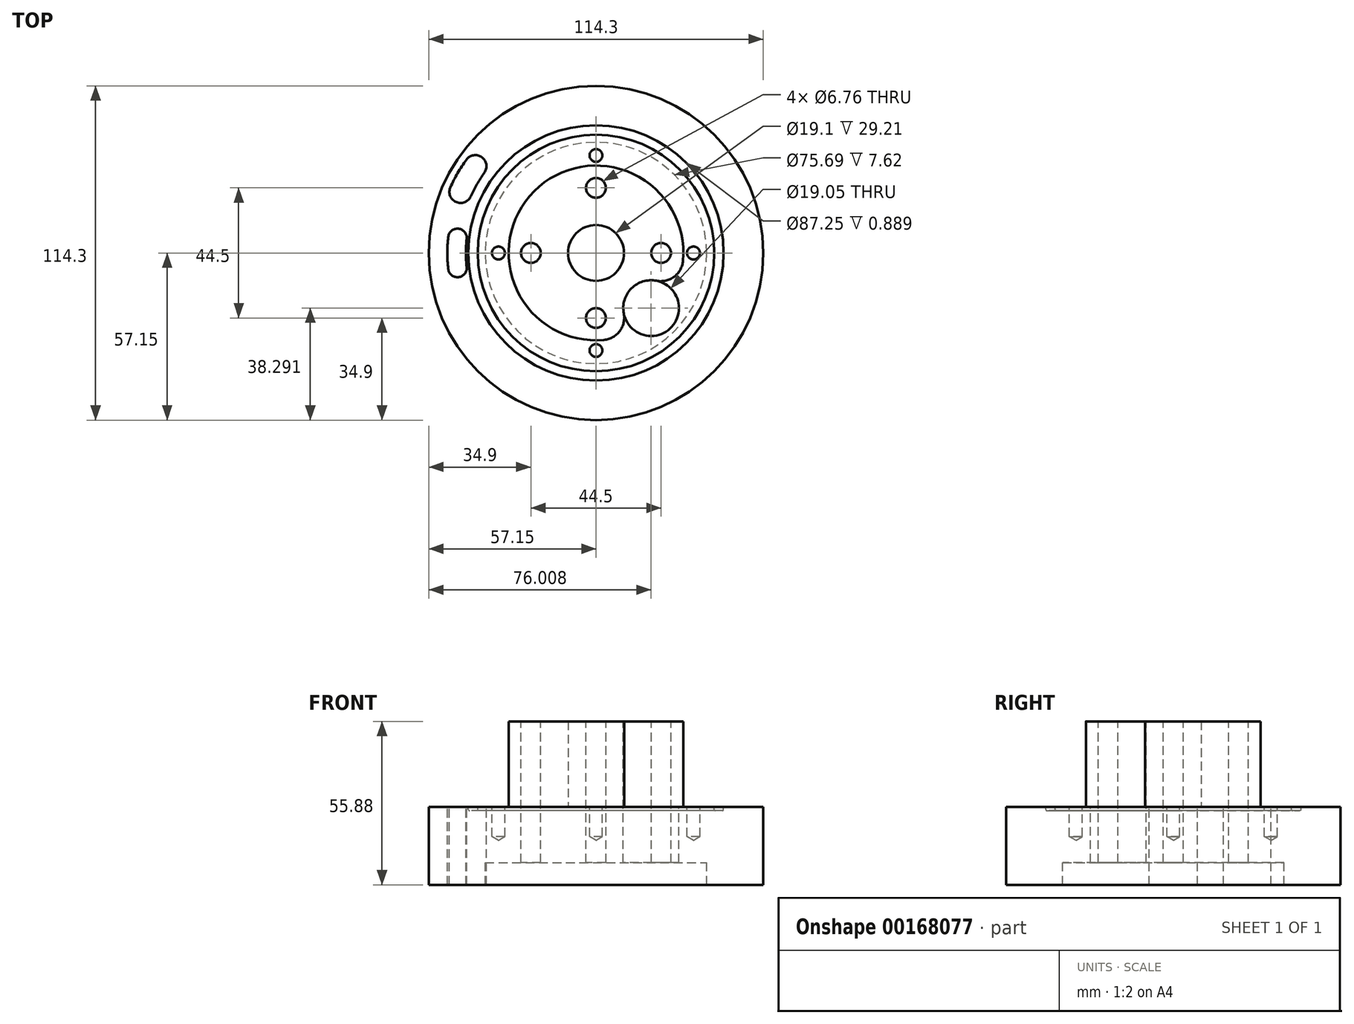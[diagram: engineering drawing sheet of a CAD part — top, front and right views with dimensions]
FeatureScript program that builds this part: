
annotation { "Feature Type Name" : "Feature", "Feature Type Description" : "" }
export const myFeature = defineFeature(function(context is Context, id is Id, definition is map)
    precondition{}
    {
        {
            var Q0;
            Q0=qCreatedBy(makeId("Top.planeOp"),FACE);
            var sketch = newSketch(context, id + "F0", { "sketchPlane" : qUnion([Q0])});
            skCircle(sketch, "E0", {"center": v(0, 0) * mm, "radius": 57.15 * mm});
            skSolve(sketch);
        }
        {
            var Q0;
            Q0=qSketchRegion(id+"F0",true);
            extrude(context, id + "F1", {"entities" : qUnion([Q0]), "depth" : 19.05 * mm});
        }
        {
            var Q0;
            Q0=makeQuery(id+"F1.opExtrude","CAP_FACE",FACE,{"disambiguationData":[OSD([sQuery(id+"F0.wireOp",EDGE,"E0")])],"isStart":false});
            var sketch = newSketch(context, id + "F2", { "sketchPlane" : qUnion([Q0])});
            skCircle(sketch, "E1", {"center": v(0, 0) * mm, "radius": 22.25 * mm, "construction": true});
            skCircle(sketch, "E2", {"center": v(0, 0) * mm, "radius": 9.55 * mm});
            skCircle(sketch, "E3", {"center": v(0, 0) * mm, "radius": 29.87 * mm});
            skSolve(sketch);
        }
        {
            var Q0;
            Q0=qSketchRegion(id+"F2",true);
            var Q1;
            Q1=qConstructionFilter(qBodyType(qCreatedBy(id+"F2",EDGE),BodyType.WIRE),ConstructionObject.NO);
            extrude(context, id + "F3", {"entities" : qUnion([Q0]), "operationType" : NewBodyOperationType.ADD, "surfaceEntities" : qUnion([Q1]), "depth" : 29.2 * mm});
        }
        {
            var Q0;
            Q0=makeQuery(id+"F3.opExtrude","CAP_FACE",FACE,{"disambiguationData":[OSD([sQuery(id+"F2.wireOp",EDGE,"E2"),sQuery(id+"F2.wireOp",EDGE,"E3")])],"isStart":false});
            var sketch = newSketch(context, id + "F4", { "sketchPlane" : qUnion([Q0])});
            skLineSegment(sketch, "E4", {"start": v(-9.55, 0) * mm, "end": v(-29.87, 0) * mm, "construction": true});
            skPoint(sketch, "E5", {"position": v(-22.25, 0) * mm});
            skPoint(sketch, "E6.1.0", {"position": v(0, -22.25) * mm});
            skPoint(sketch, "E6.2.0", {"position": v(22.25, 0) * mm});
            skPoint(sketch, "E6.3.0", {"position": v(0, 22.25) * mm});
            skPoint(sketch, "E6.center", {"position": v(0, 0) * mm});
            skSolve(sketch);
        }
        {
            var Q0;
            Q0=sQuery(id+"F4.wireOp",VERTEX,"E5");
            var Q1;
            Q1=sQuery(id+"F4.wireOp",VERTEX,"E6.3.0");
            var Q2;
            Q2=sQuery(id+"F4.wireOp",VERTEX,"E6.2.0");
            var Q3;
            Q3=sQuery(id+"F4.wireOp",VERTEX,"E6.1.0");
            var Q4;
            Q4=makeQuery(id+"F1.opExtrude","SWEPT_BODY",BODY,{"disambiguationData":[OSD([sQuery(id+"F0.wireOp",EDGE,"E0")])]});
            hole(context, id + "F5", {"style" : HoleStyle.SIMPLE, "endStyle" : HoleEndStyle.THROUGH, "standardTappedOrClearance" : lookupTablePath({ "standard" : "ANSI", "fit" : "Normal (ASME)", "size" : "1/4", "type" : "Clearance" }), "standardBlindInLast" : lookupTablePath({ "fit" : "Free", "standard" : "ANSI", "size" : "1/4", "type" : "Clearance" }), "holeDiameter" : 6.76 * mm, "locations" : qUnion([Q0, Q1, Q2, Q3]), "scope" : qUnion([Q4]), "isTappedThrough" : true});
        }
        {
            var Q0;
            Q0=makeQuery(id+"F1.opExtrude","CAP_FACE",FACE,{"disambiguationData":[OSD([sQuery(id+"F0.wireOp",EDGE,"E0")])],"isStart":true});
            var sketch = newSketch(context, id + "F6", { "sketchPlane" : qUnion([Q0])});
            skCircle(sketch, "E7", {"center": v(0, 0) * mm, "radius": 37.85 * mm});
            skCircle(sketch, "E8", {"center": v(0, 0) * mm, "radius": 57.15 * mm});
            skSolve(sketch);
        }
        {
            var Q0;
            Q0=qSketchRegion(id+"F6",true);
            extrude(context, id + "F7", {"entities" : qUnion([Q0]), "operationType" : NewBodyOperationType.ADD, "depth" : 7.62 * mm});
        }
        {
            var Q0;
            {var subQ0=sQuery(id+"F2.wireOp",EDGE,"E3");var subQ1=sQuery(id+"F2.wireOp",EDGE,"E2");Q0=makeQuery(id+"FoOJ4XAaWHjuBwS_1.boolean.opBoolean","MERGE",FACE,{"derivedFrom":[makeQuery(id+"F3.opExtrude","CAP_FACE",FACE,{"disambiguationData":[OSD([subQ1,subQ0])],"isStart":false}),makeQuery(id+"FoOJ4XAaWHjuBwS_1.opExtrude","CAP_FACE",FACE,{"disambiguationData":[OSD([subQ1,subQ0])],"isStart":false})]});}
            var sketch = newSketch(context, id + "F8", { "sketchPlane" : qUnion([Q0])});
            skPoint(sketch, "E9", {"position": v(11.13, -11.13) * mm});
            skLineSegment(sketch, "E10", {"start": v(0, 0) * mm, "end": v(11.13, -11.13) * mm, "construction": true});
            skLineSegment(sketch, "E11", {"start": v(11.13, -11.13) * mm, "end": v(18.86, -18.86) * mm, "construction": true});
            skCircle(sketch, "E12", {"center": v(18.86, -18.86) * mm, "radius": 9.53 * mm});
            skCircle(sketch, "E13.0", {"center": v(22.25, 0) * mm, "radius": 3.38 * mm, "construction": true});
            skCircle(sketch, "E14.0", {"center": v(0, -22.25) * mm, "radius": 3.38 * mm, "construction": true});
            skLineSegment(sketch, "E15", {"start": v(22.25, 0) * mm, "end": v(0, -22.25) * mm, "construction": true});
            skSolve(sketch);
        }
        {
            var Q0;
            Q0=qSketchRegion(id+"F8",true);
            extrude(context, id + "F9", {"entities" : qUnion([Q0]), "operationType" : NewBodyOperationType.REMOVE, "endBound" : BoundingType.THROUGH_ALL, "oppositeDirection" : true, "depth" : 25.4 * mm});
        }
        {
            var Q0;
            Q0=makeQuery(id+"F9.boolean.opBoolean","INTERSECT",EDGE,{"disambiguationData":[OD(0.0)],"derivedFrom":[makeQuery(id+"F3.opExtrude","SWEPT_FACE",FACE,{"disambiguationData":[OSD([sQuery(id+"F2.wireOp",EDGE,"E3")])]}),makeQuery(id+"F9.opExtrude","SWEPT_FACE",FACE,{"disambiguationData":[OSD([sQuery(id+"F8.wireOp",EDGE,"E12")])]})]});
            var Q1;
            Q1=makeQuery(id+"F9.boolean.opBoolean","INTERSECT",EDGE,{"disambiguationData":[OD(1.0)],"derivedFrom":[makeQuery(id+"F3.opExtrude","SWEPT_FACE",FACE,{"disambiguationData":[OSD([sQuery(id+"F2.wireOp",EDGE,"E3")])]}),makeQuery(id+"F9.opExtrude","SWEPT_FACE",FACE,{"disambiguationData":[OSD([sQuery(id+"F8.wireOp",EDGE,"E12")])]})]});
            var Q2;
            Q2=makeQuery(id+"FoOJ4XAaWHjuBwS_1.boolean.opBoolean","INTERSECT",EDGE,{"disambiguationData":[OD(0.0)],"derivedFrom":[makeQuery(id+"F3.opExtrude","SWEPT_FACE",FACE,{"disambiguationData":[OSD([sQuery(id+"F2.wireOp",EDGE,"E2")])]}),makeQuery(id+"FoOJ4XAaWHjuBwS_1.opExtrude","SWEPT_FACE",FACE,{"disambiguationData":[OSD([sQuery(id+"Fp6gyvLrVVLFwQT_1.wireOp",EDGE,"w4HSFiKU-dtBr-E5jh-2VqS-H0rTyRwpRXiJ")])]})]});
            var Q3;
            Q3=makeQuery(id+"FoOJ4XAaWHjuBwS_1.boolean.opBoolean","INTERSECT",EDGE,{"disambiguationData":[OD(1.0)],"derivedFrom":[makeQuery(id+"F3.opExtrude","SWEPT_FACE",FACE,{"disambiguationData":[OSD([sQuery(id+"F2.wireOp",EDGE,"E2")])]}),makeQuery(id+"FoOJ4XAaWHjuBwS_1.opExtrude","SWEPT_FACE",FACE,{"disambiguationData":[OSD([sQuery(id+"Fp6gyvLrVVLFwQT_1.wireOp",EDGE,"w4HSFiKU-dtBr-E5jh-2VqS-H0rTyRwpRXiJ")])]})]});
            fillet(context, id + "F10", {"entities" : qUnion([Q0, Q1, Q2, Q3]), "radius" : 7.62 * mm, "tangentPropagation" : true, "allowEdgeOverflow" : false});
        }
        {
            var Q0;
            {var subQ0=sQuery(id+"F0.wireOp",EDGE,"E0");Q0=makeQuery(id+"F3.boolean.opBoolean","SPLIT",FACE,{"disambiguationData":[TD([makeQuery(id+"F1.opExtrude","SWEPT_FACE",FACE,{"disambiguationData":[OSD([subQ0])]})])],"derivedFrom":makeQuery(id+"F1.opExtrude","CAP_FACE",FACE,{"disambiguationData":[OSD([subQ0])],"isStart":false})});}
            var sketch = newSketch(context, id + "F11", { "sketchPlane" : qUnion([Q0])});
            skCircle(sketch, "E16", {"center": v(0, 0) * mm, "radius": 42.02 * mm, "construction": true});
            skCircle(sketch, "E17", {"center": v(0, 0) * mm, "radius": 43.62 * mm});
            skCircle(sketch, "E18", {"center": v(0, 0) * mm, "radius": 40.42 * mm});
            skSolve(sketch);
        }
        {
            var Q0;
            Q0=qSketchRegion(id+"F11",true);
            extrude(context, id + "F12", {"entities" : qUnion([Q0]), "operationType" : NewBodyOperationType.REMOVE, "oppositeDirection" : true, "depth" : 1.3 * mm});
        }
        {
            var Q0;
            Q0=makeQuery(id+"F12.boolean.opBoolean","COPY",EDGE,{"derivedFrom":makeQuery(id+"F12.opExtrude","CAP_EDGE",EDGE,{"disambiguationData":[OSD([sQuery(id+"F11.wireOp",EDGE,"E18")])],"isStart":false})});
            var Q1;
            Q1=makeQuery(id+"F12.boolean.opBoolean","COPY",EDGE,{"derivedFrom":makeQuery(id+"F12.opExtrude","CAP_EDGE",EDGE,{"disambiguationData":[OSD([sQuery(id+"F11.wireOp",EDGE,"E17")])],"isStart":false})});
            fillet(context, id + "F13", {"entities" : qUnion([Q0, Q1]), "radius" : 0.4 * mm, "tangentPropagation" : true, "allowEdgeOverflow" : false});
        }
        {
            var Q0;
            {var subQ0=sQuery(id+"F0.wireOp",EDGE,"E0");var subQ1=makeQuery(id+"F1.opExtrude","SWEPT_FACE",FACE,{"disambiguationData":[OSD([subQ0])]});Q0=makeQuery(id+"F12.boolean.opBoolean","SPLIT",FACE,{"disambiguationData":[TD([subQ1])],"derivedFrom":makeQuery(id+"F3.boolean.opBoolean","SPLIT",FACE,{"disambiguationData":[TD([subQ1])],"derivedFrom":makeQuery(id+"F1.opExtrude","CAP_FACE",FACE,{"disambiguationData":[OSD([subQ0])],"isStart":false})})});}
            var sketch = newSketch(context, id + "F14", { "sketchPlane" : qUnion([Q0])});
            skArc(sketch, "E19", {"start": v(-43.77, 7.72) * mm, "mid": v(-44.45, 0) * mm, "end": v(-43.77, -7.72) * mm});
            skArc(sketch, "E20", {"start": v(-50.03, 8.82) * mm, "mid": v(-50.8, 0) * mm, "end": v(-50.03, -8.82) * mm});
            skLineSegment(sketch, "E21", {"start": v(-50.03, 8.82) * mm, "end": v(-43.77, 7.72) * mm});
            skLineSegment(sketch, "E22", {"start": v(-50.03, -8.82) * mm, "end": v(-43.77, -7.72) * mm});
            skLineSegment(sketch, "E23", {"start": v(-43.77, 7.72) * mm, "end": v(0, 0) * mm, "construction": true});
            skLineSegment(sketch, "E24", {"start": v(-43.77, -7.72) * mm, "end": v(0, 0) * mm, "construction": true});
            skArc(sketch, "E25", {"start": v(-44.16, 16.07) * mm, "mid": v(-40.7, 23.5) * mm, "end": v(-36, 30.2) * mm});
            skArc(sketch, "E26", {"start": v(-51.32, 18.68) * mm, "mid": v(-47.3, 27.3) * mm, "end": v(-41.83, 35.1) * mm});
            skLineSegment(sketch, "E27", {"start": v(-41.83, 35.1) * mm, "end": v(-36, 30.2) * mm});
            skLineSegment(sketch, "E28", {"start": v(-44.16, 16.07) * mm, "end": v(-51.32, 18.68) * mm});
            skLineSegment(sketch, "E29", {"start": v(-44.16, 16.07) * mm, "end": v(0, 0) * mm, "construction": true});
            skLineSegment(sketch, "E30", {"start": v(0, 0) * mm, "end": v(-36, 30.2) * mm, "construction": true});
            skPoint(sketch, "E31", {"position": v(-47.74, 17.37) * mm});
            skSolve(sketch);
        }
        {
            var Q0;
            Q0=qSketchRegion(id+"F14",true);
            extrude(context, id + "F15", {"entities" : qUnion([Q0]), "operationType" : NewBodyOperationType.REMOVE, "endBound" : BoundingType.THROUGH_ALL, "oppositeDirection" : true, "depth" : 25.4 * mm});
        }
        {
            var Q0;
            Q0=makeQuery(id+"F15.boolean.opBoolean","COPY",EDGE,{"derivedFrom":makeQuery(id+"F15.opExtrude","SWEPT_EDGE",EDGE,{"disambiguationData":[OSD([sQuery(id+"F14.wireOp",EDGE,"E26"),sQuery(id+"F14.wireOp",EDGE,"E27")])]})});
            var Q1;
            Q1=makeQuery(id+"F15.boolean.opBoolean","COPY",EDGE,{"derivedFrom":makeQuery(id+"F15.opExtrude","SWEPT_EDGE",EDGE,{"disambiguationData":[OSD([sQuery(id+"F14.wireOp",EDGE,"E25"),sQuery(id+"F14.wireOp",EDGE,"E27")])]})});
            var Q2;
            Q2=makeQuery(id+"F15.boolean.opBoolean","COPY",EDGE,{"derivedFrom":makeQuery(id+"F15.opExtrude","SWEPT_EDGE",EDGE,{"disambiguationData":[OSD([sQuery(id+"F14.wireOp",EDGE,"E25"),sQuery(id+"F14.wireOp",EDGE,"E28")])]})});
            var Q3;
            Q3=makeQuery(id+"F15.boolean.opBoolean","COPY",EDGE,{"derivedFrom":makeQuery(id+"F15.opExtrude","SWEPT_EDGE",EDGE,{"disambiguationData":[OSD([sQuery(id+"F14.wireOp",EDGE,"E26"),sQuery(id+"F14.wireOp",EDGE,"E28")])]})});
            fillet(context, id + "F16", {"entities" : qUnion([Q0, Q1, Q2, Q3]), "radius" : 3.8 * mm, "tangentPropagation" : true, "allowEdgeOverflow" : false});
        }
        {
            var Q0;
            Q0=makeQuery(id+"F15.boolean.opBoolean","COPY",EDGE,{"derivedFrom":makeQuery(id+"F15.opExtrude","SWEPT_EDGE",EDGE,{"disambiguationData":[OSD([sQuery(id+"F14.wireOp",EDGE,"E19"),sQuery(id+"F14.wireOp",EDGE,"E21")])]})});
            var Q1;
            Q1=makeQuery(id+"F15.boolean.opBoolean","COPY",EDGE,{"derivedFrom":makeQuery(id+"F15.opExtrude","SWEPT_EDGE",EDGE,{"disambiguationData":[OSD([sQuery(id+"F14.wireOp",EDGE,"E20"),sQuery(id+"F14.wireOp",EDGE,"E21")])]})});
            var Q2;
            Q2=makeQuery(id+"F15.boolean.opBoolean","COPY",EDGE,{"derivedFrom":makeQuery(id+"F15.opExtrude","SWEPT_EDGE",EDGE,{"disambiguationData":[OSD([sQuery(id+"F14.wireOp",EDGE,"E19"),sQuery(id+"F14.wireOp",EDGE,"E22")])]})});
            var Q3;
            Q3=makeQuery(id+"F15.boolean.opBoolean","COPY",EDGE,{"derivedFrom":makeQuery(id+"F15.opExtrude","SWEPT_EDGE",EDGE,{"disambiguationData":[OSD([sQuery(id+"F14.wireOp",EDGE,"E20"),sQuery(id+"F14.wireOp",EDGE,"E22")])]})});
            fillet(context, id + "F17", {"entities" : qUnion([Q0, Q1, Q2, Q3]), "radius" : 3.17 * mm, "tangentPropagation" : true, "allowEdgeOverflow" : false});
        }
        {
            var Q0;
            {var subQ2=sQuery(id+"F2.wireOp",EDGE,"E3");var subQ3=makeQuery(id+"F3.opExtrude","SWEPT_FACE",FACE,{"disambiguationData":[OSD([subQ2])]});var subQ4=sQuery(id+"F0.wireOp",EDGE,"E0");Q0=makeQuery(id+"F12.boolean.opBoolean","SPLIT",FACE,{"disambiguationData":[TD([subQ3])],"derivedFrom":makeQuery(id+"F3.boolean.opBoolean","SPLIT",FACE,{"disambiguationData":[TD([makeQuery(id+"F1.opExtrude","SWEPT_FACE",FACE,{"disambiguationData":[OSD([subQ4])]})])],"derivedFrom":makeQuery(id+"F1.opExtrude","CAP_FACE",FACE,{"disambiguationData":[OSD([subQ4])],"isStart":false})})});}
            var sketch = newSketch(context, id + "F18", { "sketchPlane" : qUnion([Q0])});
            skLineSegment(sketch, "E32", {"start": v(0, 0) * mm, "end": v(33.34, 0) * mm, "construction": true});
            skPoint(sketch, "E33", {"position": v(33.34, 0) * mm});
            skPoint(sketch, "E34.1.0", {"position": v(0, 33.34) * mm});
            skPoint(sketch, "E34.2.0", {"position": v(-33.34, 0) * mm});
            skPoint(sketch, "E34.3.0", {"position": v(0, -33.34) * mm});
            skPoint(sketch, "E34.center", {"position": v(0, 0) * mm});
            skSolve(sketch);
        }
        {
            var Q0;
            Q0=sQuery(id+"F18.wireOp",VERTEX,"E33");
            var Q1;
            Q1=sQuery(id+"F18.wireOp",VERTEX,"E34.3.0");
            var Q2;
            Q2=sQuery(id+"F18.wireOp",VERTEX,"E34.2.0");
            var Q3;
            Q3=sQuery(id+"F18.wireOp",VERTEX,"E34.1.0");
            var Q4;
            Q4=makeQuery(id+"F1.opExtrude","SWEPT_BODY",BODY,{"disambiguationData":[OSD([sQuery(id+"F0.wireOp",EDGE,"E0")])]});
            hole(context, id + "F19", {"style" : HoleStyle.SIMPLE, "endStyle" : HoleEndStyle.BLIND, "holeDiameter" : 4.4 * mm, "holeDepth" : 10.16 * mm, "locations" : qUnion([Q0, Q1, Q2, Q3]), "scope" : qUnion([Q4])});
        }
    });
